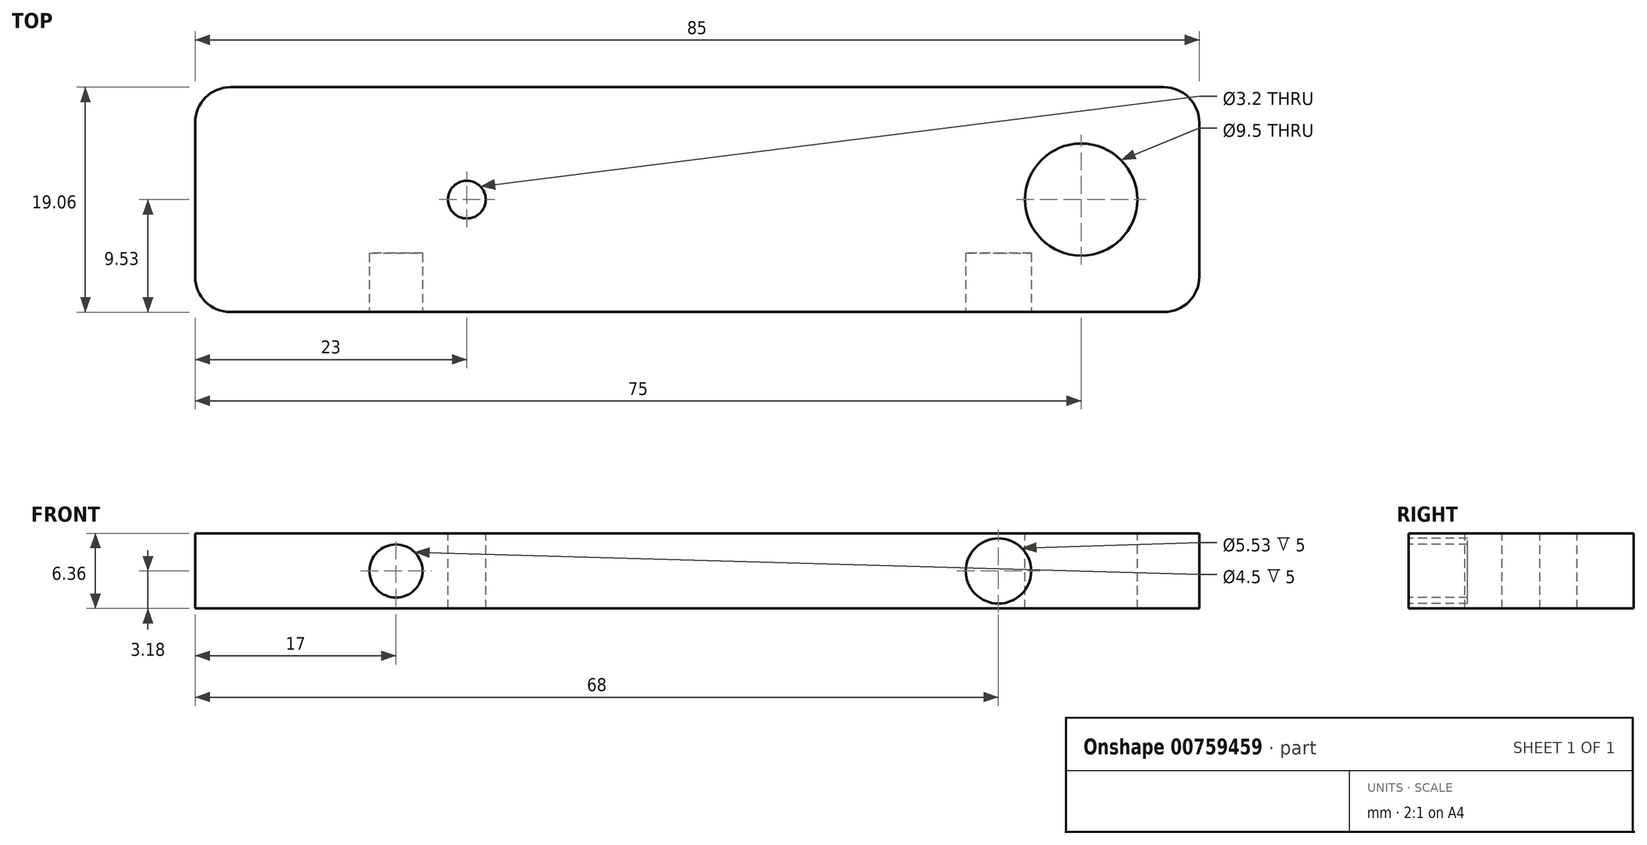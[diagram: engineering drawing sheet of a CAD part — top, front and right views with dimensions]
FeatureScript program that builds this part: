
annotation { "Feature Type Name" : "Feature", "Feature Type Description" : "" }
export const myFeature = defineFeature(function(context is Context, id is Id, definition is map)
    precondition{}
    {
        {
            var Q0;
            Q0=qCreatedBy(makeId("Top.planeOp"),FACE);
            var sketch = newSketch(context, id + "F0", { "sketchPlane" : qUnion([Q0])});
            skLineSegment(sketch, "E0.bottom", {"start": v(42.5, 9.53) * mm, "end": v(-42.5, 9.53) * mm});
            skLineSegment(sketch, "E0.top", {"start": v(42.5, -9.53) * mm, "end": v(-42.5, -9.53) * mm});
            skLineSegment(sketch, "E0.left", {"start": v(42.5, 9.53) * mm, "end": v(42.5, -9.53) * mm});
            skLineSegment(sketch, "E0.right", {"start": v(-42.5, 9.52) * mm, "end": v(-42.5, -9.53) * mm});
            skPoint(sketch, "E0.middle", {"position": v(0, 0) * mm});
            skCircle(sketch, "E1", {"center": v(-19.5, 0) * mm, "radius": 1.6 * mm});
            skCircle(sketch, "E2", {"center": v(32.5, 0) * mm, "radius": 4.75 * mm});
            skSolve(sketch);
        }
        {
            var Q0;
            Q0=makeQuery(id+"F0.imprint","IMPRINT",FACE,{"disambiguationData":[TD([[makeQuery(id+"F0.imprint","IMPRINT",EDGE,{"derivedFrom":sQuery(id+"F0.wireOp",EDGE,"E0.bottom")}),1.0]])]});
            extrude(context, id + "F1", {"entities" : qUnion([Q0]), "endBound" : BoundingType.SYMMETRIC, "oppositeDirection" : true, "depth" : 6.35 * mm, "offsetDistance" : 25 * mm});
        }
        {
            var Q0;
            Q0=makeQuery(id+"F1.opExtrude","SWEPT_FACE",FACE,{"disambiguationData":[OSD([sQuery(id+"F0.wireOp",EDGE,"E0.top")])]});
            var sketch = newSketch(context, id + "F2", { "sketchPlane" : qUnion([Q0])});
            skCircle(sketch, "E3", {"center": v(-25.5, 0) * mm, "radius": 2.25 * mm});
            skCircle(sketch, "E4", {"center": v(25.5, 0) * mm, "radius": 2.77 * mm});
            skSolve(sketch);
        }
        {
            var Q0;
            Q0=makeQuery(id+"F2.imprint","IMPRINT",FACE,{"disambiguationData":[TD([[makeQuery(id+"F2.imprint","IMPRINT",EDGE,{"derivedFrom":sQuery(id+"F2.wireOp",EDGE,"E3")}),1.0]])]});
            var Q1;
            Q1=makeQuery(id+"F2.imprint","IMPRINT",FACE,{"disambiguationData":[TD([[makeQuery(id+"F2.imprint","IMPRINT",EDGE,{"derivedFrom":sQuery(id+"F2.wireOp",EDGE,"E4")}),1.0]])]});
            extrude(context, id + "F3", {"entities" : qUnion([Q0, Q1]), "operationType" : NewBodyOperationType.REMOVE, "oppositeDirection" : true, "depth" : 5 * mm, "offsetDistance" : 25 * mm});
        }
        {
            var Q0;
            Q0=makeQuery(id+"F1.opExtrude","SWEPT_EDGE",EDGE,{"disambiguationData":[OSD([sQuery(id+"F0.wireOp",EDGE,"E0.top"),sQuery(id+"F0.wireOp",EDGE,"E0.left")])]});
            var Q1;
            Q1=makeQuery(id+"F1.opExtrude","SWEPT_EDGE",EDGE,{"disambiguationData":[OSD([sQuery(id+"F0.wireOp",EDGE,"E0.bottom"),sQuery(id+"F0.wireOp",EDGE,"E0.left")])]});
            var Q2;
            Q2=makeQuery(id+"F1.opExtrude","SWEPT_EDGE",EDGE,{"disambiguationData":[OSD([sQuery(id+"F0.wireOp",EDGE,"E0.top"),sQuery(id+"F0.wireOp",EDGE,"E0.right")])]});
            var Q3;
            Q3=makeQuery(id+"F1.opExtrude","SWEPT_EDGE",EDGE,{"disambiguationData":[OSD([sQuery(id+"F0.wireOp",EDGE,"E0.bottom"),sQuery(id+"F0.wireOp",EDGE,"E0.right")])]});
            fillet(context, id + "F4", {"entities" : qUnion([Q0, Q1, Q2, Q3]), "radius" : 3 * mm, "tangentPropagation" : true, "allowEdgeOverflow" : false});
        }
    });
